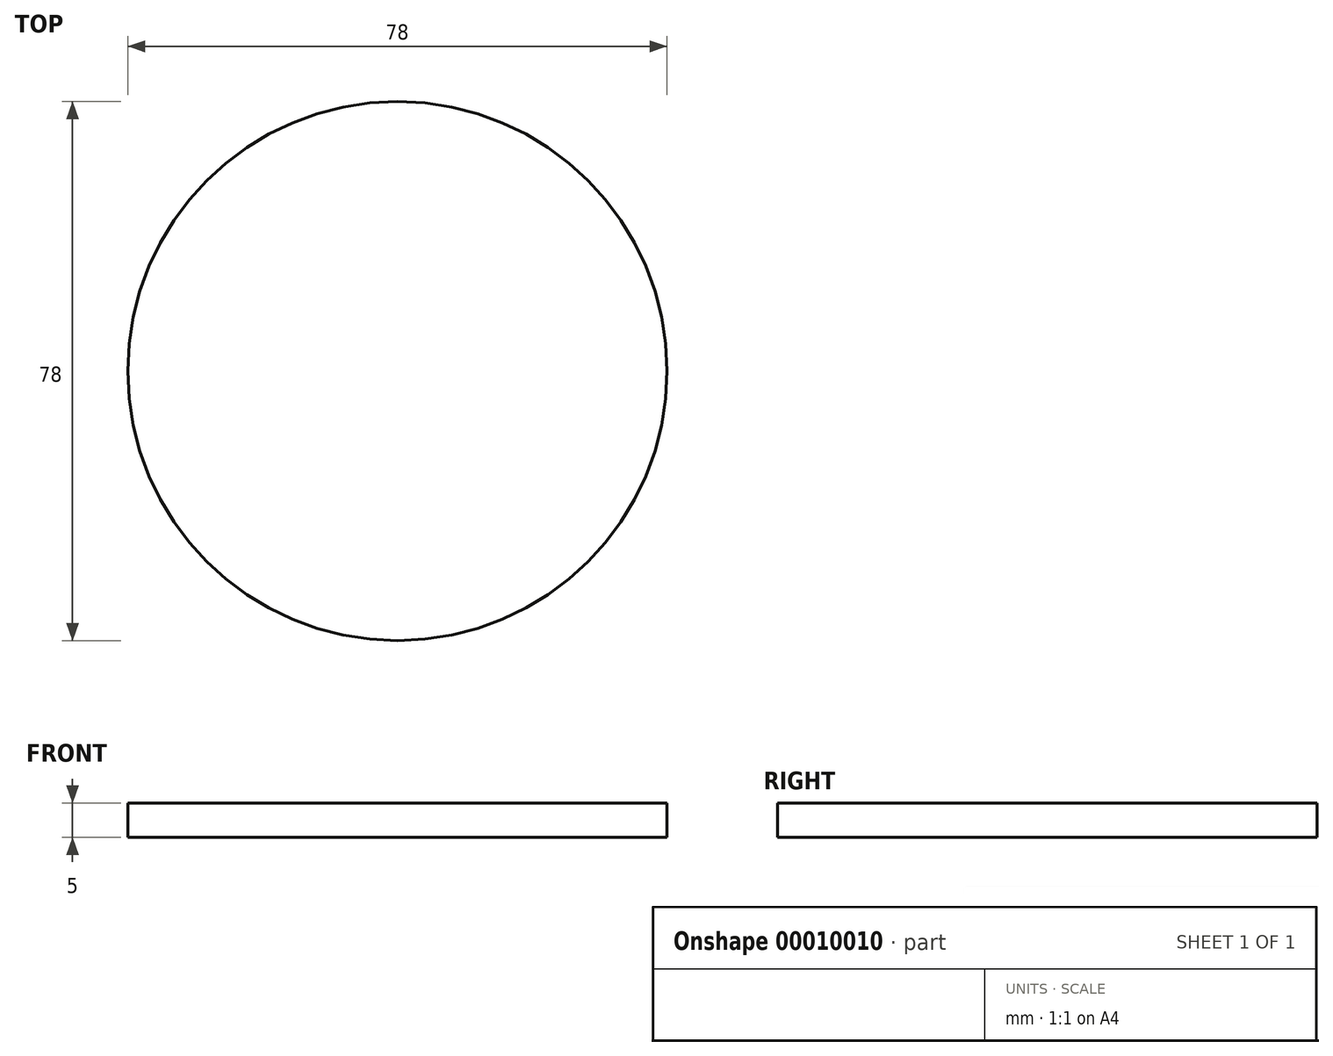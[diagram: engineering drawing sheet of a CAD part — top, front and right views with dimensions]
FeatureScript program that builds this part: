
annotation { "Feature Type Name" : "Feature", "Feature Type Description" : "" }
export const myFeature = defineFeature(function(context is Context, id is Id, definition is map)
    precondition{}
    {
        {
            var Q0;
            Q0=qCreatedBy(makeId("Top.planeOp"),FACE);
            var sketch = newSketch(context, id + "F0", { "sketchPlane" : qUnion([Q0])});
            skCircle(sketch, "E0", {"center": v(0.43, -0.99) * mm, "radius": 39 * mm});
            skSolve(sketch);
        }
        {
            var Q0;
            Q0 = qSketchRegion(id + "F0", true);
            extrude(context, id + "F1", {"entities" : qUnion([Q0]), "depth" : 5 * mm});
        }
    });
